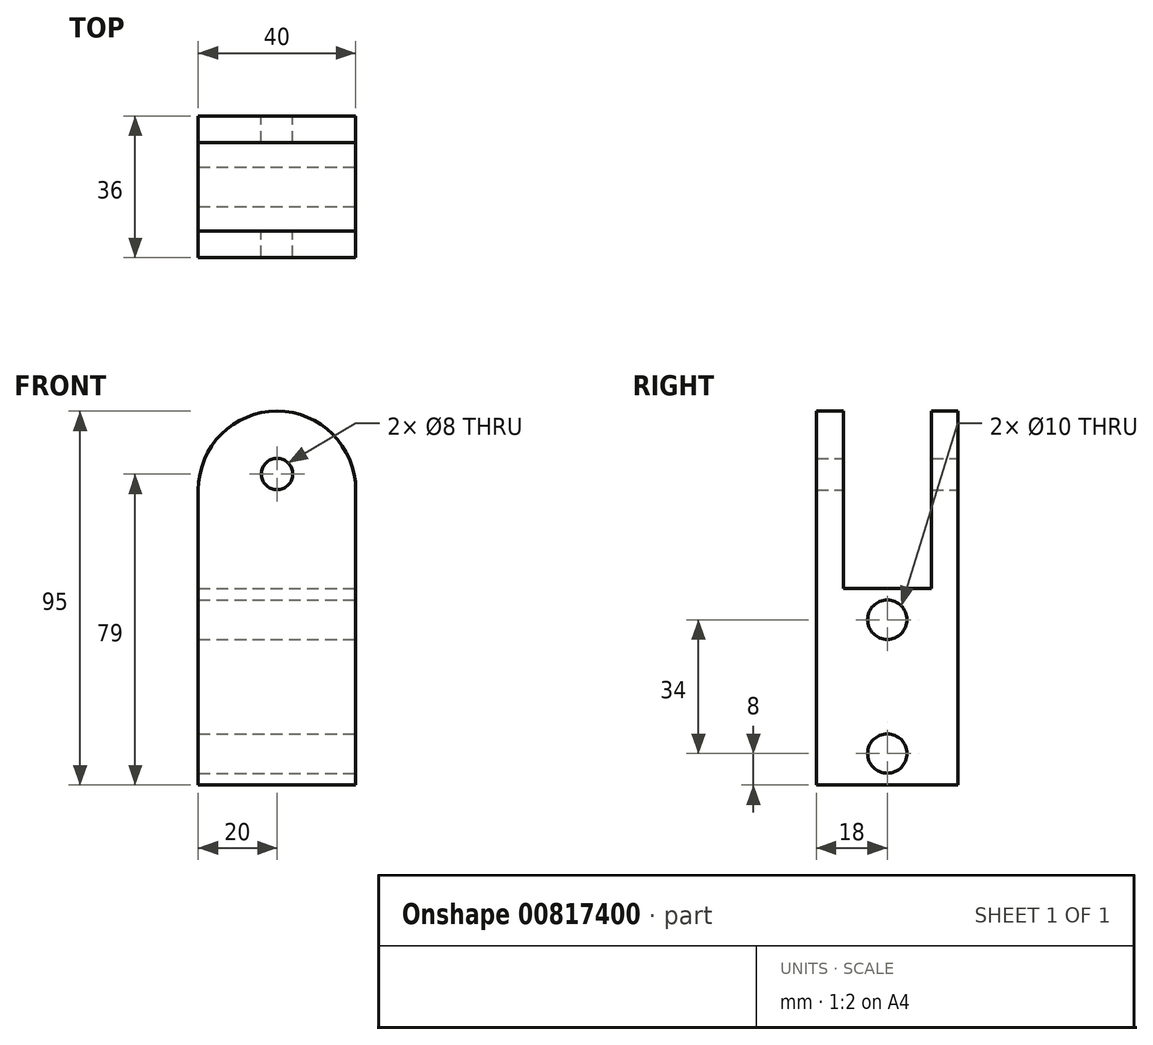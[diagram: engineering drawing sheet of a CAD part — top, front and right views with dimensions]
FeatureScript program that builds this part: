
annotation { "Feature Type Name" : "Feature", "Feature Type Description" : "" }
export const myFeature = defineFeature(function(context is Context, id is Id, definition is map)
    precondition{}
    {
        {
            var Q0;
            Q0=qCreatedBy(makeId("Top.planeOp"),FACE);
            var sketch = newSketch(context, id + "F0", { "sketchPlane" : qUnion([Q0])});
            skLineSegment(sketch, "E0.bottom", {"start": v(20, -18) * mm, "end": v(-20, -18) * mm});
            skLineSegment(sketch, "E0.top", {"start": v(20, 18) * mm, "end": v(-20, 18) * mm});
            skLineSegment(sketch, "E0.left", {"start": v(20, -18) * mm, "end": v(20, 18) * mm});
            skLineSegment(sketch, "E0.right", {"start": v(-20, -18) * mm, "end": v(-20, 18) * mm});
            skPoint(sketch, "E0.middle", {"position": v(0, 0) * mm});
            skSolve(sketch);
        }
        {
            var Q0;
            Q0=makeQuery(id+"F0.imprint","IMPRINT",FACE,{"disambiguationData":[TD([[makeQuery(id+"F0.imprint","IMPRINT",EDGE,{"derivedFrom":sQuery(id+"F0.wireOp",EDGE,"E0.bottom")}),-1.0]])]});
            extrude(context, id + "F1", {"entities" : qUnion([Q0]), "depth" : 50 * mm, "offsetDistance" : 25 * mm});
        }
        {
            var Q0;
            Q0=makeQuery(id+"F1.opExtrude","SWEPT_FACE",FACE,{"disambiguationData":[OSD([sQuery(id+"F0.wireOp",EDGE,"E0.left")])]});
            var sketch = newSketch(context, id + "F2", { "sketchPlane" : qUnion([Q0])});
            skCircle(sketch, "E1", {"center": v(0, 8) * mm, "radius": 5 * mm});
            skPoint(sketch, "E1.centerSnap0", {"position": v(0, 0) * mm});
            skCircle(sketch, "E2", {"center": v(0, 42) * mm, "radius": 5 * mm});
            skLineSegment(sketch, "E3", {"start": v(-18, 25) * mm, "end": v(18, 25) * mm});
            skSolve(sketch);
        }
        {
            var Q0;
            Q0=makeQuery(id+"F2.imprint","IMPRINT",FACE,{"disambiguationData":[TD([[makeQuery(id+"F2.imprint","IMPRINT",EDGE,{"derivedFrom":sQuery(id+"F2.wireOp",EDGE,"E2")}),1.0]])]});
            var Q1;
            Q1=makeQuery(id+"F2.imprint","IMPRINT",FACE,{"disambiguationData":[TD([[makeQuery(id+"F2.imprint","IMPRINT",EDGE,{"derivedFrom":sQuery(id+"F2.wireOp",EDGE,"E1")}),1.0]])]});
            extrude(context, id + "F3", {"entities" : qUnion([Q0, Q1]), "operationType" : NewBodyOperationType.REMOVE, "oppositeDirection" : true, "depth" : 45 * mm, "offsetDistance" : 25 * mm});
        }
        {
            var Q0;
            Q0=makeQuery(id+"F1.opExtrude","CAP_FACE",FACE,{"disambiguationData":[OSD([sQuery(id+"F0.wireOp",EDGE,"E0.bottom"),sQuery(id+"F0.wireOp",EDGE,"E0.top"),sQuery(id+"F0.wireOp",EDGE,"E0.left"),sQuery(id+"F0.wireOp",EDGE,"E0.right")])],"isStart":false});
            var sketch = newSketch(context, id + "F4", { "sketchPlane" : qUnion([Q0])});
            skLineSegment(sketch, "E4.bottom", {"start": v(-20, -18) * mm, "end": v(20, -18) * mm});
            skLineSegment(sketch, "E4.top", {"start": v(-20, -11.2) * mm, "end": v(20, -11.2) * mm});
            skLineSegment(sketch, "E4.left", {"start": v(-20, -18) * mm, "end": v(-20, -11.2) * mm});
            skLineSegment(sketch, "E4.right", {"start": v(20, -18) * mm, "end": v(20, -11.2) * mm});
            skLineSegment(sketch, "E5.bottom", {"start": v(-20, 18) * mm, "end": v(20, 18) * mm});
            skLineSegment(sketch, "E5.top", {"start": v(-20, 11.2) * mm, "end": v(20, 11.2) * mm});
            skLineSegment(sketch, "E5.left", {"start": v(-20, 18) * mm, "end": v(-20, 11.2) * mm});
            skLineSegment(sketch, "E5.right", {"start": v(20, 18) * mm, "end": v(20, 11.2) * mm});
            skSolve(sketch);
        }
        {
            var Q0;
            Q0=makeQuery(id+"F4.imprint","IMPRINT",FACE,{"disambiguationData":[TD([[makeQuery(id+"F4.imprint","IMPRINT",EDGE,{"derivedFrom":sQuery(id+"F4.wireOp",EDGE,"E4.bottom")}),-1.0]])]});
            var Q1;
            Q1=makeQuery(id+"F4.imprint","IMPRINT",FACE,{"disambiguationData":[TD([[makeQuery(id+"F4.imprint","IMPRINT",EDGE,{"derivedFrom":sQuery(id+"F4.wireOp",EDGE,"E5.bottom")}),1.0]])]});
            extrude(context, id + "F5", {"entities" : qUnion([Q0, Q1]), "operationType" : NewBodyOperationType.ADD, "depth" : 45 * mm, "offsetDistance" : 25 * mm});
        }
        {
            var Q0;
            Q0=makeQuery(id+"F5.opExtrude","CAP_EDGE",EDGE,{"disambiguationData":[OSD([sQuery(id+"F4.wireOp",EDGE,"E5.right")])],"isStart":false});
            var Q1;
            Q1=makeQuery(id+"F5.opExtrude","CAP_EDGE",EDGE,{"disambiguationData":[OSD([sQuery(id+"F4.wireOp",EDGE,"E4.right")])],"isStart":false});
            var Q2;
            Q2=makeQuery(id+"F5.opExtrude","CAP_EDGE",EDGE,{"disambiguationData":[OSD([sQuery(id+"F4.wireOp",EDGE,"E5.left")])],"isStart":false});
            var Q3;
            Q3=makeQuery(id+"F5.opExtrude","CAP_EDGE",EDGE,{"disambiguationData":[OSD([sQuery(id+"F4.wireOp",EDGE,"E4.left")])],"isStart":false});
            fillet(context, id + "F6", {"entities" : qUnion([Q0, Q1, Q2, Q3]), "radius" : 20 * mm, "tangentPropagation" : true, "allowEdgeOverflow" : false});
        }
        {
            var Q0;
            Q0=makeQuery(id+"F5.boolean.opBoolean","MERGE",FACE,{"derivedFrom":[makeQuery(id+"F1.opExtrude","SWEPT_FACE",FACE,{"disambiguationData":[OSD([sQuery(id+"F0.wireOp",EDGE,"E0.top")])]}),makeQuery(id+"F5.opExtrude","SWEPT_FACE",FACE,{"disambiguationData":[OSD([sQuery(id+"F4.wireOp",EDGE,"E5.bottom")])]})]});
            var sketch = newSketch(context, id + "F7", { "sketchPlane" : qUnion([Q0])});
            skCircle(sketch, "E6", {"center": v(0, 79) * mm, "radius": 4 * mm});
            skSolve(sketch);
        }
        {
            var Q0;
            Q0=makeQuery(id+"F7.imprint","IMPRINT",FACE,{"disambiguationData":[TD([[makeQuery(id+"F7.imprint","IMPRINT",EDGE,{"derivedFrom":sQuery(id+"F7.wireOp",EDGE,"E6")}),1.0]])]});
            extrude(context, id + "F8", {"entities" : qUnion([Q0]), "operationType" : NewBodyOperationType.REMOVE, "oppositeDirection" : true, "depth" : 50 * mm, "offsetDistance" : 25 * mm});
        }
    });
